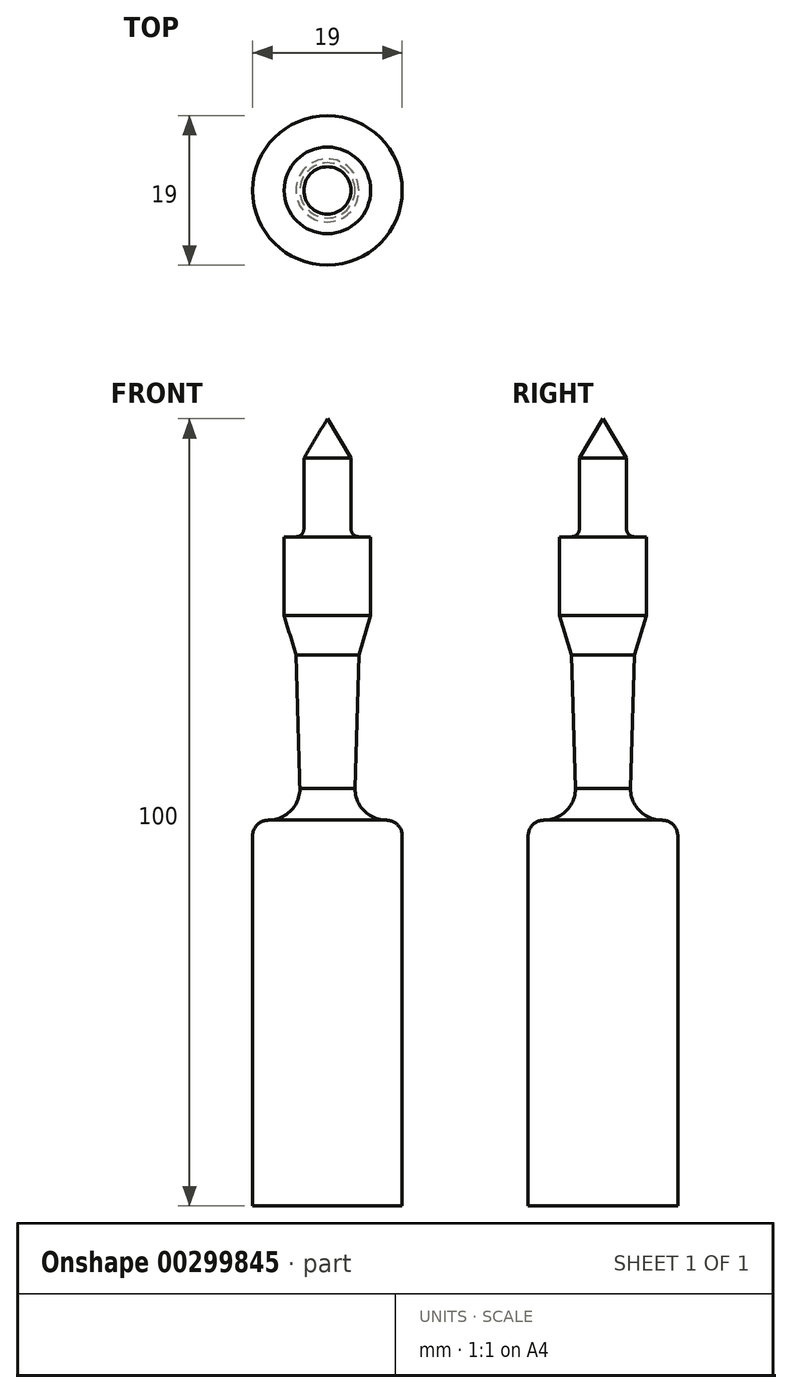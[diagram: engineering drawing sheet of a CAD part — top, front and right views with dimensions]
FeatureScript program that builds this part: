
annotation { "Feature Type Name" : "Feature", "Feature Type Description" : "" }
export const myFeature = defineFeature(function(context is Context, id is Id, definition is map)
    precondition{}
    {
        {
            var Q0;
            Q0=qCreatedBy(makeId("Front.planeOp"),FACE);
            var sketch = newSketch(context, id + "F0", { "sketchPlane" : qUnion([Q0])});
            skLineSegment(sketch, "E0", {"start": v(0, 0) * mm, "end": v(3, -5) * mm});
            skLineSegment(sketch, "E1", {"start": v(3, -5) * mm, "end": v(3, -14) * mm});
            skArc(sketch, "E2", {"start": v(3, -14) * mm, "mid": v(3.3, -14.7) * mm, "end": v(4, -15) * mm});
            skLineSegment(sketch, "E3", {"start": v(4, -15) * mm, "end": v(5.5, -15) * mm});
            skLineSegment(sketch, "E4", {"start": v(5.5, -15) * mm, "end": v(5.5, -25) * mm});
            skLineSegment(sketch, "E5", {"start": v(5.5, -25) * mm, "end": v(4, -30) * mm});
            skArc(sketch, "E6", {"start": v(3.5, -47) * mm, "mid": v(4.67, -49.83) * mm, "end": v(7.5, -51) * mm});
            skArc(sketch, "E7", {"start": v(9.5, -53) * mm, "mid": v(8.91, -51.59) * mm, "end": v(7.5, -51) * mm});
            skLineSegment(sketch, "E8", {"start": v(9.5, -53) * mm, "end": v(9.5, -100) * mm});
            skLineSegment(sketch, "E9", {"start": v(9.5, -100) * mm, "end": v(0, -100) * mm});
            skLineSegment(sketch, "E10", {"start": v(0, -100) * mm, "end": v(0, 0) * mm});
            skLineSegment(sketch, "E11", {"start": v(4, -30) * mm, "end": v(3.5, -47) * mm});
            skSolve(sketch);
        }
        {
            var Q0;
            Q0=makeQuery(id+"F0.imprint","IMPRINT",FACE,{"disambiguationData":[TD([[makeQuery(id+"F0.imprint","IMPRINT",EDGE,{"derivedFrom":sQuery(id+"F0.wireOp",EDGE,"E0")}),-1.0]])]});
            var Q1;
            Q1=sQuery(id+"F0.wireOp",EDGE,"E10");
            revolve(context, id + "F1", {"entities" : qUnion([Q0]), "axis" : qUnion([Q1]), "revolveType" : RevolveType.FULL});
        }
    });
